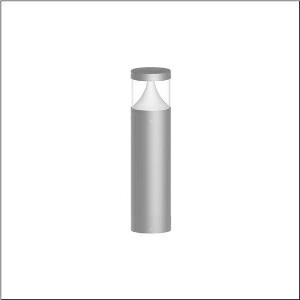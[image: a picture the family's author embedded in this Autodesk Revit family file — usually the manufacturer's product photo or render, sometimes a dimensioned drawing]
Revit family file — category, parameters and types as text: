
# Revit family: cl_31_poller_60_5cl434603
name_source: partatom
category: Lighting Fixtures
units: mm (PartAtom-declared; Revit-internal decimal feet)

## family parameters
Cut with Voids When Loaded = No
Host = Face
Light Source = No
Part Type = Normal
Room Calculation Point = No
Round Connector Dimension = Use Diameter
Shared = No

## types (1)
- --- (1 x LED, 1500 lm, 14 W, 3000K)
    Apparent Load = 14 VA
    CIE Flux Codes = 19 66 88 92 100
    Color Rendering = 80
    Color Temperature = 3000K
    Default Elevation = 1800 mm
    Description = CL 31 Bollard 60, bollard luminaire, primary light control with lens, of PC, primary optical cover: cover panel, of PC, transparent, secondary light control with reflector, of PC, primary light characteristic: asymmetric, LED, rated luminous flux: 1.500lm, luminous efficacy: 107lm/W, light colour: 830, colour temperature: 3000K, control gear: ECG DALI, with terminal, 5-pole, max. 2.5mm², mains connection: 220..240V, AC, 50/60Hz, rated input power: 14W, luminaire housing, of aluminium, powder-coated, Siteco® metallic grey, diameter: 170mm, height: 600mm, protection rating (complete): IP65, insulation class (complete): insulation class I (protective earthing), certification: CE, ENEC, impact resistance: IK10, permissible operating ambient temperature for outdoor applications: -20..+50°C, packaging unit: 1 piece
    Height = 200 mm  [stored 0.656168 ft]
    Lamp = 1 x LED
    Lamp Light Flux = 1500 lm
    Lamp Power = 14 W
    Lamp count = 1
    Length = 170 mm  [stored 0.557743 ft]
    Luminous efficacy = 107 lm/W
    Manufacturer = Siteco
    ModVariant = No
    Model = 5CL434603
    Mounting Place = Floor
    Mounting Type = Freestanding
    Number of Poles = 1
    OnlyDefault = Yes
    Power Factor = 1
    Product Name = CL 31 Poller 60
    Product group = bollard luminaire
    ProductGroupID = 1304
    Protection Class = Protection class I
    Protection Degree = IP 65
    RLX_Detail_Level = 1
    RLX_Emergency_Light_Flux = 0 lm
    RLX_Emergency_Type = 0
    RLX_Emergency_Type_DB = No
    RlxData = <blob elided: 63529 chars, md5=541eeac0>
    Socket = socket
    Standby Power = 0 W
    System Light Flux = 1500 lm
    System Power = 14 W
    Type Comments = factory setting: luminous flux: 100 % | dim-lin: 254 | 350 mA
    Type Image = l_1006903.jpg
    URL = http://relux.com
    VarID = @adj_130369
    Voltage = 0 V
    Weight = 0.00 kg
    Width = 0 mm  [stored 0 ft]

note: [stored X ft] marks values corroborated as IEEE doubles in the binary element streams (Revit-internal decimal feet)

## geometry (parser evidence)
native form markers: Blend x4, Sweep x13
no freeform markers — native parametric forms only
